# Revit family: LAMP_CORNER 48V
name_source: partatom
category: Mobiliario
revit_build: Autodesk Revit 2015 (Build: 20140606_1530(x64)
units: mm (PartAtom-declared; Revit-internal decimal feet)

## types (4) — shared parameters
Accessory Type = Assembly
Fabricante = LAMP
Installation instructions = https://www.lamp.es
Last update = 12/04/2019
Manufacturer URL = http://www.lamp.es
Manufacturer country = Spain
Manufacturer name = LAMP
Product URL = https://www.lamp.es
Product datasheet = http://www.lamp.es
Weight = 0.23 kg

## per-type parameters (varying)
| type | Descripción | Finish | Material | Modelo | Product code |
| IN BLACK | TRACK 48V ACC. IN 90º CORNER DALI BK. | RAL9011 textured | LAMP_Aluminio Carril NG | TLSULIDB | TLSULIDB |
| IN WHITE | TRACK 48V ACC. IN 90º CORNER DALI WH. | RAL9010 textured | LAMP_Aluminio Carril BL | TLSULIDW | TLSULIDW |
| OUT BLACK | TRACK 48V ACC. OUT 90º CORNER DALI BK. | RAL9011 textured | LAMP_Aluminio Carril NG | TLSULODB | TLSULODB |
| OUT WHITE | TRACK 48V ACC. OUT 90º CORNER DALI WH. | RAL9010 textured | LAMP_Aluminio Carril BL | TLSULODW | TLSULODW |
